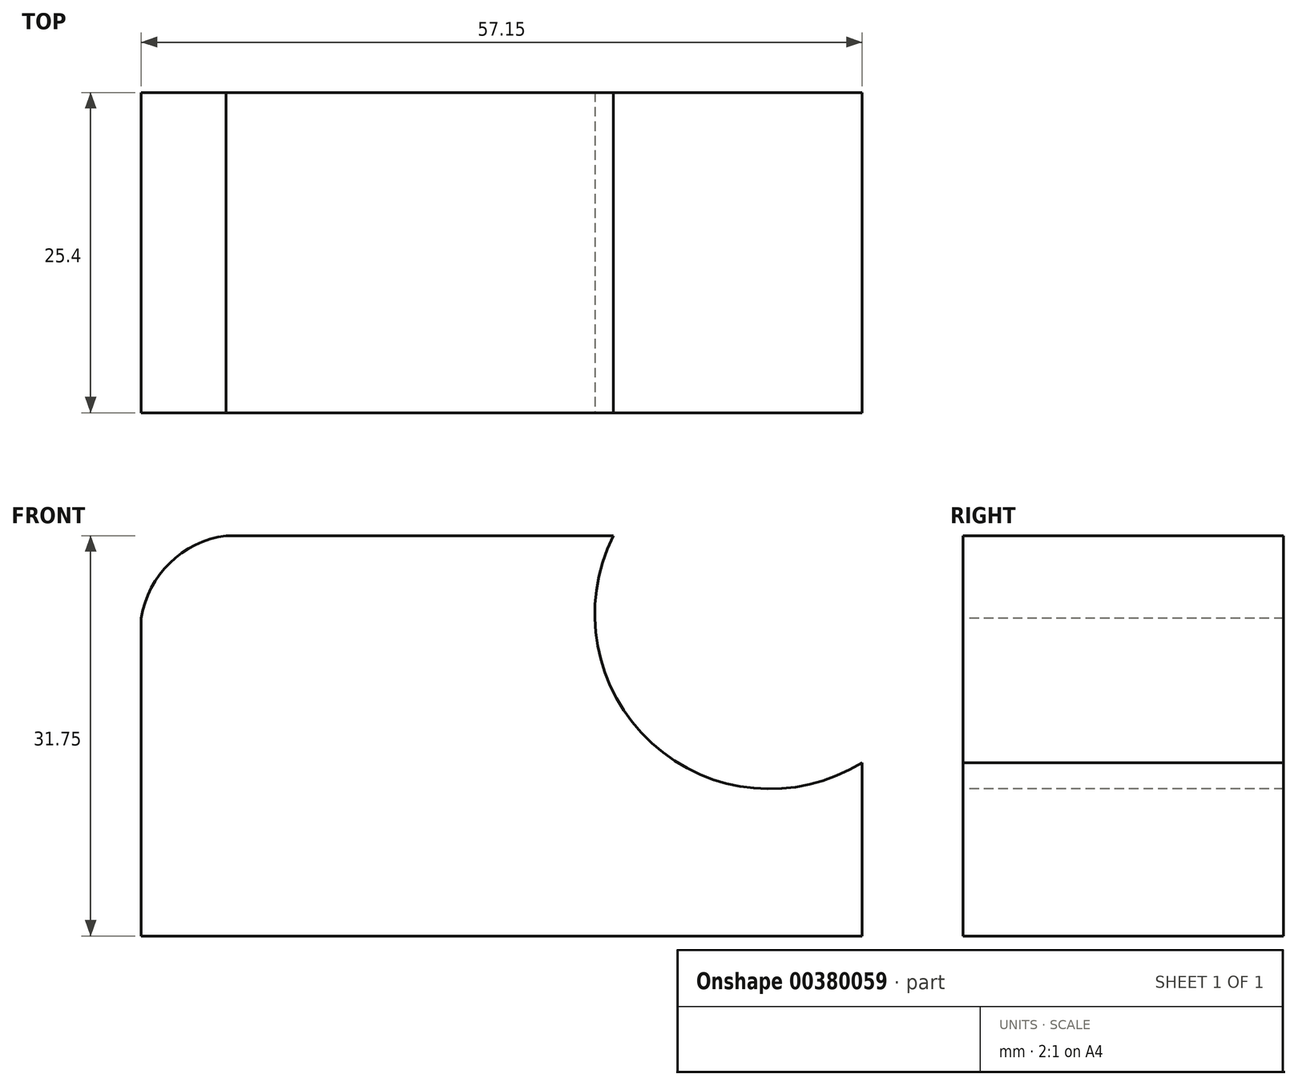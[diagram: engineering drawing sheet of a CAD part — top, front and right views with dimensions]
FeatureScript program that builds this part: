
annotation { "Feature Type Name" : "Feature", "Feature Type Description" : "" }
export const myFeature = defineFeature(function(context is Context, id is Id, definition is map)
    precondition{}
    {
        {
            var Q0;
            Q0=qCreatedBy(makeId("Front.planeOp"),FACE);
            var sketch = newSketch(context, id + "F0", { "sketchPlane" : qUnion([Q0])});
            skLineSegment(sketch, "E0", {"start": v(0, 0) * mm, "end": v(0, 31.75) * mm});
            skLineSegment(sketch, "E1", {"start": v(0, 31.75) * mm, "end": v(57.15, 31.75) * mm});
            skLineSegment(sketch, "E2", {"start": v(57.15, 31.75) * mm, "end": v(57.15, 0) * mm});
            skLineSegment(sketch, "E3", {"start": v(57.15, 0) * mm, "end": v(0, 0) * mm});
            skSolve(sketch);
        }
        {
            var Q0;
            Q0=makeQuery(id+"F0.imprint","IMPRINT",FACE,{"disambiguationData":[TD([[makeQuery(id+"F0.imprint","IMPRINT",EDGE,{"derivedFrom":sQuery(id+"F0.wireOp",EDGE,"E0")}),-1.0]])]});
            extrude(context, id + "F1", {"entities" : qUnion([Q0]), "depth" : 25.4 * mm});
        }
        {
            var Q0;
            Q0=makeQuery(id+"F1.opExtrude","CAP_FACE",FACE,{"disambiguationData":[OSD([sQuery(id+"F0.wireOp",EDGE,"E0"),sQuery(id+"F0.wireOp",EDGE,"E1"),sQuery(id+"F0.wireOp",EDGE,"E2"),sQuery(id+"F0.wireOp",EDGE,"E3")])],"isStart":false});
            var sketch = newSketch(context, id + "F2", { "sketchPlane" : qUnion([Q0])});
            skCircle(sketch, "E4", {"center": v(7.74, 23.99) * mm, "radius": 7.83 * mm});
            skCircle(sketch, "E5", {"center": v(50.39, 25.51) * mm, "radius": 13.19 * mm});
            skSolve(sketch);
        }
        {
            var Q0;
            {var subQ0=sQuery(id+"F2.wireOp",EDGE,"E4");var subQ1=makeQuery(id+"F1.opExtrude","CAP_EDGE",EDGE,{"disambiguationData":[OSD([sQuery(id+"F0.wireOp",EDGE,"E1")])],"isStart":false});var subQ2=makeQuery(id+"F2.imprint","INTERSECT",VERTEX,{"disambiguationData":[OD(0.0)],"derivedFrom":[subQ1,subQ0]});Q0=makeQuery(id+"F2.imprint","IMPRINT",FACE,{"disambiguationData":[TD([[makeQuery(id+"F2.imprint","IMPRINT",EDGE,{"disambiguationData":[TD([[subQ2,-1.0]])],"derivedFrom":subQ0}),-1.0]])]});}
            var Q1;
            {var subQ0=sQuery(id+"F2.wireOp",EDGE,"Dy8MoMjC-0H2a-IV3X-yc8l-5sC4DytuGIBn");var subQ1=makeQuery(id+"F1.opExtrude","CAP_EDGE",EDGE,{"disambiguationData":[OSD([sQuery(id+"F0.wireOp",EDGE,"E2")])],"isStart":false});var subQ2=makeQuery(id+"F2.imprint","INTERSECT",VERTEX,{"disambiguationData":[OD(0.0)],"derivedFrom":[subQ1,subQ0]});Q1=makeQuery(id+"F2.imprint","IMPRINT",FACE,{"disambiguationData":[TD([[makeQuery(id+"F2.imprint","IMPRINT",EDGE,{"disambiguationData":[TD([[subQ2,-1.0]])],"derivedFrom":subQ0}),1.0]])]});}
            var Q2;
            Q2=sQuery(id+"F2.wireOp",EDGE,"Dy8MoMjC-0H2a-IV3X-yc8l-5sC4DytuGIBn");
            extrude(context, id + "F3", {"entities" : qUnion([Q0, Q1]), "operationType" : NewBodyOperationType.REMOVE, "surfaceEntities" : qUnion([Q2]), "oppositeDirection" : true, "depth" : 25.4 * mm});
        }
        {
            var Q0;
            Q0=makeQuery(id+"F1.opExtrude","CAP_FACE",FACE,{"disambiguationData":[OSD([sQuery(id+"F0.wireOp",EDGE,"E0"),sQuery(id+"F0.wireOp",EDGE,"E1"),sQuery(id+"F0.wireOp",EDGE,"E2"),sQuery(id+"F0.wireOp",EDGE,"E3")])],"isStart":false});
            var sketch = newSketch(context, id + "F4", { "sketchPlane" : qUnion([Q0])});
            skSolve(sketch);
        }
        {
            var Q0;
            Q0=makeQuery(id+"F4.imprint","IMPRINT",FACE,{"disambiguationData":[TD([[makeQuery(id+"F4.imprint","IMPRINT",EDGE,{"derivedFrom":makeQuery(id+"F1.opExtrude","CAP_EDGE",EDGE,{"disambiguationData":[OSD([sQuery(id+"F0.wireOp",EDGE,"E2")])],"isStart":false})}),-1.0]])]});
            var sketch = newSketch(context, id + "F5", { "sketchPlane" : qUnion([Q0])});
            skCircle(sketch, "E6", {"center": v(49.83, 25.54) * mm, "radius": 13.87 * mm});
            skSolve(sketch);
        }
        {
            var Q0;
            Q0 = qSketchRegion(id + "F5", true);
            extrude(context, id + "F6", {"entities" : qUnion([Q0]), "operationType" : NewBodyOperationType.REMOVE, "oppositeDirection" : true, "depth" : 25.4 * mm});
        }
    });
